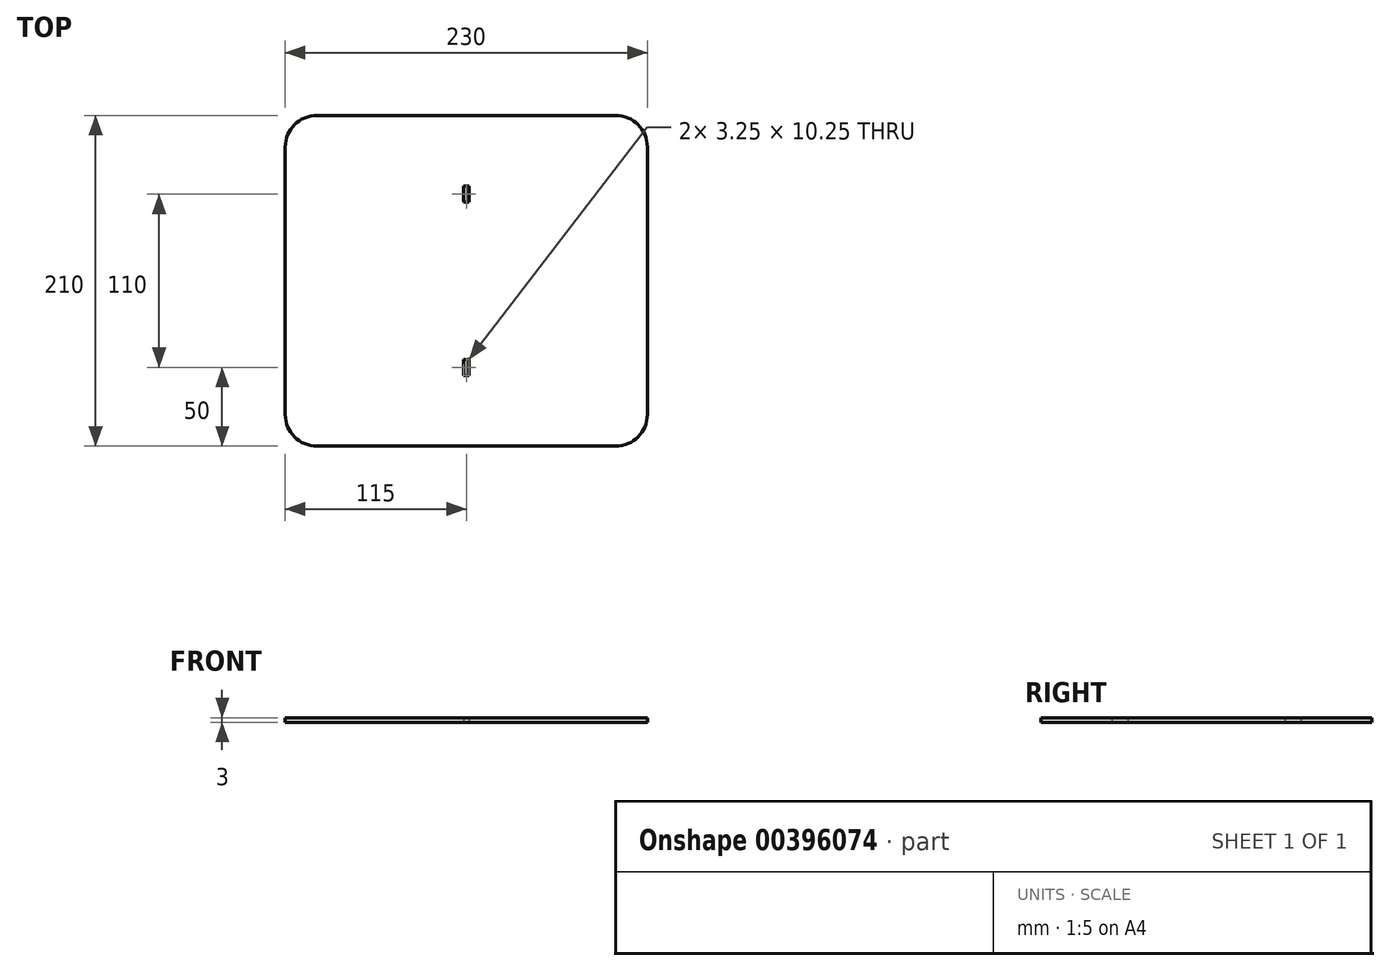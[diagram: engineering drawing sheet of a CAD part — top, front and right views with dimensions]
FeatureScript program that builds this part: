
annotation { "Feature Type Name" : "Feature", "Feature Type Description" : "" }
export const myFeature = defineFeature(function(context is Context, id is Id, definition is map)
    precondition{}
    {
        {
            var Q0;
            Q0=qCreatedBy(makeId("Top.planeOp"),FACE);
            var sketch = newSketch(context, id + "F0", { "sketchPlane" : qUnion([Q0])});
            skLineSegment(sketch, "E0.bottom", {"start": v(-95, 105) * mm, "end": v(95, 105) * mm});
            skLineSegment(sketch, "E0.top", {"start": v(-95, -105) * mm, "end": v(95, -105) * mm});
            skLineSegment(sketch, "E0.left", {"start": v(-115, 85) * mm, "end": v(-115, -85) * mm});
            skLineSegment(sketch, "E0.right", {"start": v(115, 85) * mm, "end": v(115, -85) * mm});
            skPoint(sketch, "E0.middle", {"position": v(0, 0) * mm});
            skPoint(sketch, "E1.visualSharp", {"position": v(-115, 105) * mm});
            skArc(sketch, "E1.filletArc", {"start": v(-95, 105) * mm, "mid": v(-109.14, 99.14) * mm, "end": v(-115, 85) * mm});
            skPoint(sketch, "E2.visualSharp", {"position": v(-115, -105) * mm});
            skArc(sketch, "E2.filletArc", {"start": v(-115, -85) * mm, "mid": v(-109.14, -99.14) * mm, "end": v(-95, -105) * mm});
            skPoint(sketch, "E3.visualSharp", {"position": v(115, -105) * mm});
            skArc(sketch, "E3.filletArc", {"start": v(95, -105) * mm, "mid": v(109.14, -99.14) * mm, "end": v(115, -85) * mm});
            skPoint(sketch, "E4.visualSharp", {"position": v(115, 105) * mm});
            skArc(sketch, "E4.filletArc", {"start": v(115, 85) * mm, "mid": v(109.14, 99.14) * mm, "end": v(95, 105) * mm});
            skPoint(sketch, "E5.bottom.start.orphan", {"position": v(-125, 85) * mm});
            skPoint(sketch, "E5.right.start.orphan", {"position": v(125, 85) * mm});
            skPoint(sketch, "E5.top.end.orphan", {"position": v(125, -85) * mm});
            skPoint(sketch, "E5.top.start.orphan", {"position": v(-125, -85) * mm});
            skLineSegment(sketch, "E6", {"start": v(0, 105) * mm, "end": v(0, -105) * mm, "construction": true});
            skLineSegment(sketch, "E7", {"start": v(-115, 0) * mm, "end": v(115, 0) * mm, "construction": true});
            skLineSegment(sketch, "E8.bottom", {"start": v(-1.62, 60.12) * mm, "end": v(1.63, 60.12) * mm});
            skLineSegment(sketch, "E8.top", {"start": v(-1.62, 49.87) * mm, "end": v(1.63, 49.87) * mm});
            skLineSegment(sketch, "E8.left", {"start": v(-1.62, 60.12) * mm, "end": v(-1.62, 49.87) * mm});
            skLineSegment(sketch, "E8.right", {"start": v(1.63, 60.12) * mm, "end": v(1.63, 49.87) * mm});
            skPoint(sketch, "E8.middle", {"position": v(0, 55) * mm});
            skLineSegment(sketch, "E9.MirrorCS", {"start": v(1.63, -60.13) * mm, "end": v(1.63, -49.88) * mm});
            skLineSegment(sketch, "E10.MirrorCS", {"start": v(-1.62, -60.13) * mm, "end": v(-1.62, -49.88) * mm});
            skLineSegment(sketch, "E11.MirrorCS", {"start": v(-1.62, -60.13) * mm, "end": v(1.63, -60.13) * mm});
            skLineSegment(sketch, "E12.MirrorCS", {"start": v(-1.62, -49.88) * mm, "end": v(1.63, -49.88) * mm});
            skSolve(sketch);
        }
        {
            var Q0;
            Q0=qSketchRegion(id+"F0",true);
            extrude(context, id + "F1", {"entities" : qUnion([Q0]), "depth" : 3 * mm});
        }
    });
